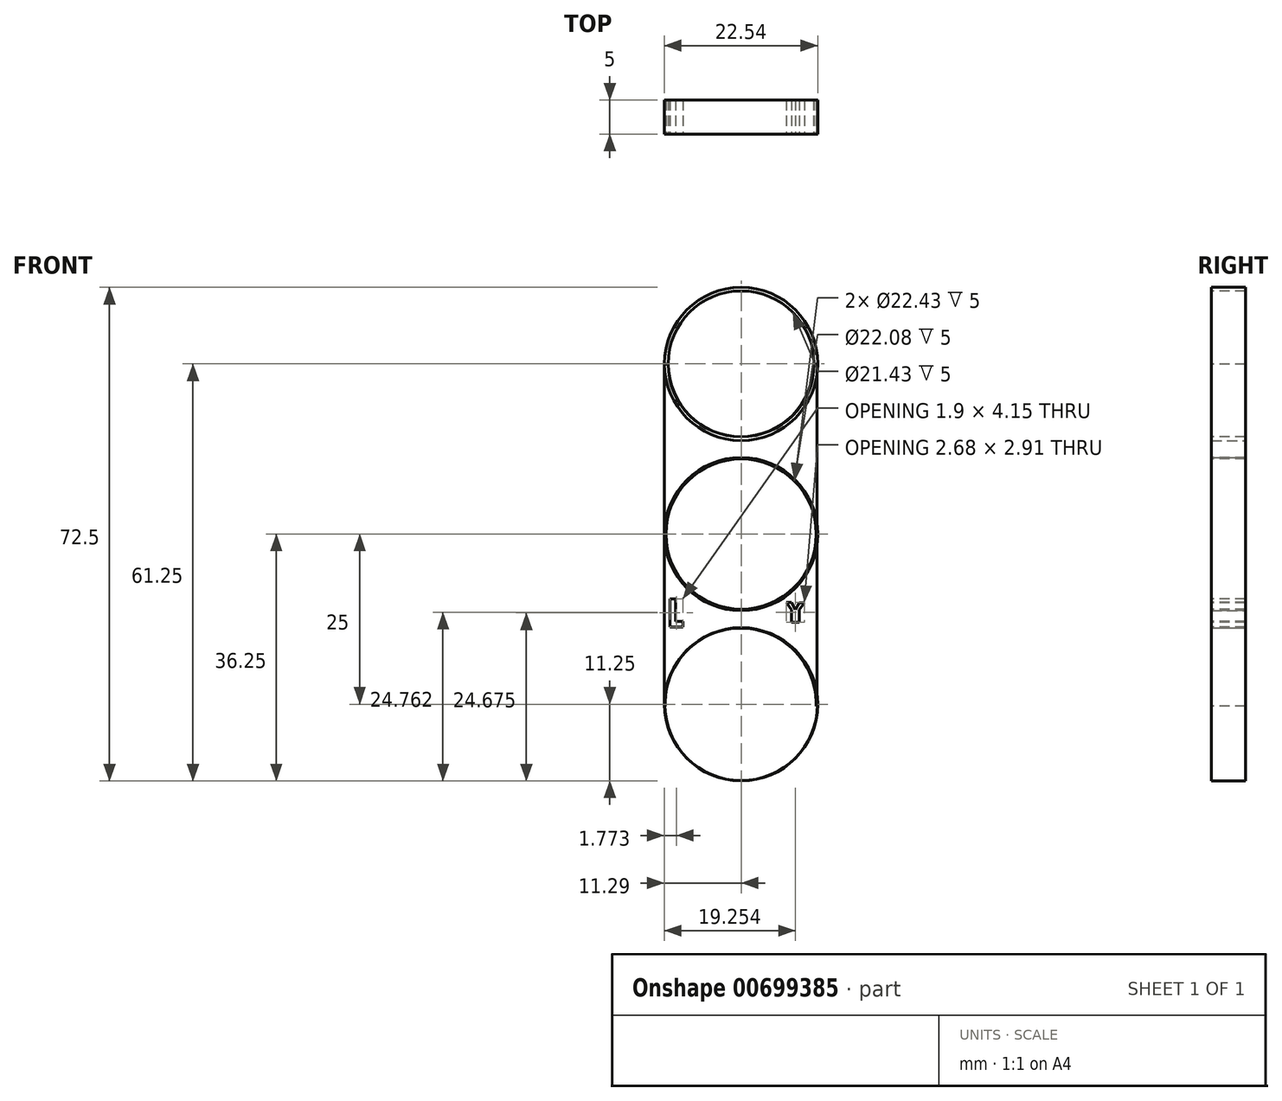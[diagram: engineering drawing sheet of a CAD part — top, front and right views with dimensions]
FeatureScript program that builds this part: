
annotation { "Feature Type Name" : "Feature", "Feature Type Description" : "" }
export const myFeature = defineFeature(function(context is Context, id is Id, definition is map)
    precondition{}
    {
        {
            var Q0;
            Q0=qCreatedBy(makeId("Front.planeOp"),FACE);
            var sketch = newSketch(context, id + "F0", { "sketchPlane" : qUnion([Q0])});
            skCircle(sketch, "E0", {"center": v(0, 25) * mm, "radius": 11.25 * mm});
            skCircle(sketch, "E1", {"center": v(0, 0) * mm, "radius": 11.25 * mm});
            skCircle(sketch, "E2", {"center": v(0, -25) * mm, "radius": 11.25 * mm});
            skSolve(sketch);
        }
        {
            var Q0;
            Q0=makeQuery(id+"F0.imprint","IMPRINT",FACE,{"disambiguationData":[TD([[makeQuery(id+"F0.imprint","IMPRINT",EDGE,{"derivedFrom":sQuery(id+"F0.wireOp",EDGE,"E0")}),1.0]])]});
            var Q1;
            Q1=makeQuery(id+"F0.imprint","IMPRINT",FACE,{"disambiguationData":[TD([[makeQuery(id+"F0.imprint","IMPRINT",EDGE,{"derivedFrom":sQuery(id+"F0.wireOp",EDGE,"E1")}),1.0]])]});
            var Q2;
            Q2=makeQuery(id+"F0.imprint","IMPRINT",FACE,{"disambiguationData":[TD([[makeQuery(id+"F0.imprint","IMPRINT",EDGE,{"derivedFrom":sQuery(id+"F0.wireOp",EDGE,"E2")}),1.0]])]});
            extrude(context, id + "F1", {"entities" : qUnion([Q0, Q1, Q2]), "depth" : 5 * mm, "offsetDistance" : 25 * mm});
        }
        {
            var Q0;
            Q0=makeQuery(id+"F1.opExtrude","CAP_FACE",FACE,{"disambiguationData":[OSD([sQuery(id+"F0.wireOp",EDGE,"E0")])],"isStart":false});
            var sketch = newSketch(context, id + "F2", { "sketchPlane" : qUnion([Q0])});
            skCircle(sketch, "E3", {"center": v(0, 25) * mm, "radius": 10.71 * mm});
            skSolve(sketch);
        }
        {
            var Q0;
            Q0 = qSketchRegion(id + "F2", true);
            extrude(context, id + "F3", {"entities" : qUnion([Q0]), "operationType" : NewBodyOperationType.REMOVE, "oppositeDirection" : true, "depth" : 25 * mm, "offsetDistance" : 25 * mm});
        }
        {
            var Q0;
            Q0=makeQuery(id+"F1.opExtrude","CAP_FACE",FACE,{"disambiguationData":[OSD([sQuery(id+"F0.wireOp",EDGE,"E1")])],"isStart":false});
            var sketch = newSketch(context, id + "F4", { "sketchPlane" : qUnion([Q0])});
            skCircle(sketch, "E4", {"center": v(0, 0) * mm, "radius": 11.21 * mm});
            skSolve(sketch);
        }
        {
            var Q0;
            Q0 = qSketchRegion(id + "F4", true);
            extrude(context, id + "F5", {"entities" : qUnion([Q0]), "operationType" : NewBodyOperationType.REMOVE, "oppositeDirection" : true, "depth" : 25 * mm, "offsetDistance" : 25 * mm});
        }
        {
            var Q0;
            Q0=makeQuery(id+"F1.opExtrude","CAP_FACE",FACE,{"disambiguationData":[OSD([sQuery(id+"F0.wireOp",EDGE,"E2")])],"isStart":false});
            var sketch = newSketch(context, id + "F6", { "sketchPlane" : qUnion([Q0])});
            skCircle(sketch, "E5", {"center": v(0, -25) * mm, "radius": 11.21 * mm});
            skSolve(sketch);
        }
        {
            var Q0;
            Q0 = qSketchRegion(id + "F6", true);
            extrude(context, id + "F7", {"entities" : qUnion([Q0]), "operationType" : NewBodyOperationType.REMOVE, "oppositeDirection" : true, "depth" : 25 * mm, "offsetDistance" : 25 * mm});
        }
        {
            var Q0;
            Q0=qCreatedBy(makeId("Front.planeOp"),FACE);
            var sketch = newSketch(context, id + "F8", { "sketchPlane" : qUnion([Q0])});
            skLineSegment(sketch, "E6", {"start": v(-11.29, 24.95) * mm, "end": v(-11.29, -25.3) * mm});
            skLineSegment(sketch, "E7", {"start": v(11.15, 24.95) * mm, "end": v(11.15, -25.3) * mm});
            skLineSegment(sketch, "E8", {"start": v(-11.29, -25.3) * mm, "end": v(11.15, -25.3) * mm});
            skLineSegment(sketch, "E9", {"start": v(-11.29, 24.95) * mm, "end": v(11.15, 24.95) * mm});
            skSolve(sketch);
        }
        {
            var Q0;
            Q0 = qSketchRegion(id + "F8", true);
            extrude(context, id + "F9", {"entities" : qUnion([Q0]), "depth" : 5 * mm, "offsetDistance" : 25 * mm});
        }
        {
            var Q0;
            Q0=makeQuery(id+"F9.opExtrude","CAP_FACE",FACE,{"disambiguationData":[OSD([sQuery(id+"F8.wireOp",EDGE,"E6"),sQuery(id+"F8.wireOp",EDGE,"E7"),sQuery(id+"F8.wireOp",EDGE,"E8"),sQuery(id+"F8.wireOp",EDGE,"E9")])],"isStart":false});
            var sketch = newSketch(context, id + "F10", { "sketchPlane" : qUnion([Q0])});
            skArc(sketch, "E10", {"start": v(-10.67, 24.95) * mm, "mid": v(-0.03, 14.3) * mm, "end": v(10.62, 24.95) * mm});
            skLineSegment(sketch, "E11", {"start": v(-10.67, 24.95) * mm, "end": v(10.62, 24.95) * mm});
            skSolve(sketch);
        }
        {
            var Q0;
            Q0 = qSketchRegion(id + "F10", true);
            extrude(context, id + "F11", {"entities" : qUnion([Q0]), "operationType" : NewBodyOperationType.REMOVE, "oppositeDirection" : true, "depth" : 25 * mm, "offsetDistance" : 25 * mm});
        }
        {
            var Q0;
            Q0=makeQuery(id+"F9.opExtrude","CAP_FACE",FACE,{"disambiguationData":[OSD([sQuery(id+"F8.wireOp",EDGE,"E6"),sQuery(id+"F8.wireOp",EDGE,"E7"),sQuery(id+"F8.wireOp",EDGE,"E8"),sQuery(id+"F8.wireOp",EDGE,"E9")])],"isStart":false});
            var sketch = newSketch(context, id + "F12", { "sketchPlane" : qUnion([Q0])});
            skCircle(sketch, "E12", {"center": v(0, 0) * mm, "radius": 11.04 * mm});
            skSolve(sketch);
        }
        {
            var Q0;
            Q0 = qSketchRegion(id + "F12", true);
            extrude(context, id + "F13", {"entities" : qUnion([Q0]), "operationType" : NewBodyOperationType.REMOVE, "oppositeDirection" : true, "depth" : 25 * mm, "offsetDistance" : 25 * mm});
        }
        {
            var Q0;
            Q0=makeQuery(id+"F9.opExtrude","CAP_FACE",FACE,{"disambiguationData":[OSD([sQuery(id+"F8.wireOp",EDGE,"E6"),sQuery(id+"F8.wireOp",EDGE,"E7"),sQuery(id+"F8.wireOp",EDGE,"E8"),sQuery(id+"F8.wireOp",EDGE,"E9")])],"isStart":false});
            var sketch = newSketch(context, id + "F14", { "sketchPlane" : qUnion([Q0])});
            skArc(sketch, "E13", {"start": v(11.02, -25.3) * mm, "mid": v(-0.07, -13.82) * mm, "end": v(-11.17, -25.3) * mm});
            skLineSegment(sketch, "E14", {"start": v(-11.17, -25.3) * mm, "end": v(11.02, -25.3) * mm});
            skSolve(sketch);
        }
        {
            var Q0;
            Q0 = qSketchRegion(id + "F14", true);
            extrude(context, id + "F15", {"entities" : qUnion([Q0]), "operationType" : NewBodyOperationType.REMOVE, "oppositeDirection" : true, "depth" : 25 * mm, "offsetDistance" : 25 * mm});
        }
        {
            var Q0;
            Q0=makeQuery(id+"F9.opExtrude","CAP_FACE",FACE,{"disambiguationData":[OSD([sQuery(id+"F8.wireOp",EDGE,"E6"),sQuery(id+"F8.wireOp",EDGE,"E7"),sQuery(id+"F8.wireOp",EDGE,"E8"),sQuery(id+"F8.wireOp",EDGE,"E9")])],"isStart":false});
            var sketch = newSketch(context, id + "F16", { "sketchPlane" : qUnion([Q0])});
            skLineSegment(sketch, "E15", {"start": v(-10.47, -9.5) * mm, "end": v(-10.47, -13.65) * mm});
            skLineSegment(sketch, "E16", {"start": v(-10.47, -13.65) * mm, "end": v(-8.57, -13.65) * mm});
            skLineSegment(sketch, "E17", {"start": v(-8.57, -13.65) * mm, "end": v(-8.57, -12.82) * mm});
            skLineSegment(sketch, "E18", {"start": v(-8.57, -12.82) * mm, "end": v(-9.6, -12.82) * mm});
            skLineSegment(sketch, "E19", {"start": v(-9.6, -12.82) * mm, "end": v(-9.6, -9.5) * mm});
            skLineSegment(sketch, "E20", {"start": v(-9.6, -9.5) * mm, "end": v(-10.47, -9.5) * mm});
            skSolve(sketch);
        }
        {
            var Q0;
            Q0 = qSketchRegion(id + "F16", true);
            extrude(context, id + "F17", {"entities" : qUnion([Q0]), "operationType" : NewBodyOperationType.REMOVE, "oppositeDirection" : true, "depth" : 25 * mm, "offsetDistance" : 25 * mm});
        }
        {
            var Q0;
            Q0=makeQuery(id+"F9.opExtrude","CAP_FACE",FACE,{"disambiguationData":[OSD([sQuery(id+"F8.wireOp",EDGE,"E6"),sQuery(id+"F8.wireOp",EDGE,"E7"),sQuery(id+"F8.wireOp",EDGE,"E8"),sQuery(id+"F8.wireOp",EDGE,"E9")])],"isStart":false});
            var sketch = newSketch(context, id + "F18", { "sketchPlane" : qUnion([Q0])});
            skLineSegment(sketch, "E21", {"start": v(6.62, -10.04) * mm, "end": v(7.4, -10.04) * mm});
            skLineSegment(sketch, "E22", {"start": v(7.4, -10.04) * mm, "end": v(7.96, -11.1) * mm});
            skLineSegment(sketch, "E23", {"start": v(7.96, -11.1) * mm, "end": v(8.52, -10.1) * mm});
            skLineSegment(sketch, "E24", {"start": v(8.52, -10.1) * mm, "end": v(9.3, -10.1) * mm});
            skLineSegment(sketch, "E25", {"start": v(9.3, -10.1) * mm, "end": v(8.52, -11.1) * mm});
            skLineSegment(sketch, "E26", {"start": v(8.52, -11.1) * mm, "end": v(8.52, -12.94) * mm});
            skLineSegment(sketch, "E27", {"start": v(8.52, -12.94) * mm, "end": v(7.4, -12.94) * mm});
            skLineSegment(sketch, "E28", {"start": v(7.4, -12.94) * mm, "end": v(7.4, -11.1) * mm});
            skLineSegment(sketch, "E29", {"start": v(7.4, -11.1) * mm, "end": v(6.62, -10.04) * mm});
            skSolve(sketch);
        }
        {
            var Q0;
            Q0 = qSketchRegion(id + "F18", true);
            extrude(context, id + "F19", {"entities" : qUnion([Q0]), "operationType" : NewBodyOperationType.REMOVE, "oppositeDirection" : true, "depth" : 25 * mm, "offsetDistance" : 25 * mm});
        }
    });
